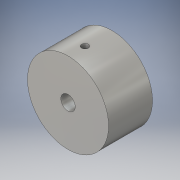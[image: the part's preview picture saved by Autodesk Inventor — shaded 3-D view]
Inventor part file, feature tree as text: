
AUTODESK INVENTOR PART (.ipt)
format: ipt  version: 2016 (Build 200138000, 138)  size: 115,200 bytes
history: native  units: in
note: dims shown in document units (in); Inventor stores cm internally (conversion verified against a paired STEP export)
features: extrude x2, sketch x2
ambient origin geometry x8: Origin, YZ Plane, XZ Plane, XY Plane, X Axis, Y Axis, Z Axis, Center Point
bodies: Solid1 (feature_tree)
feature tree (4):
  extrude  "Extrusion1"  Depth=0.252in
  extrude  "Extrusion2"  Depth=0.4724in
  sketch  "Sketch1"  dims[d0=1.4173in d1=0.252in]
  sketch  "Sketch2"  dims[d2=0.7677in d3=0.0in d4=0.4724in d5=0.1181in d6=1.4173in d7=0.0in]
